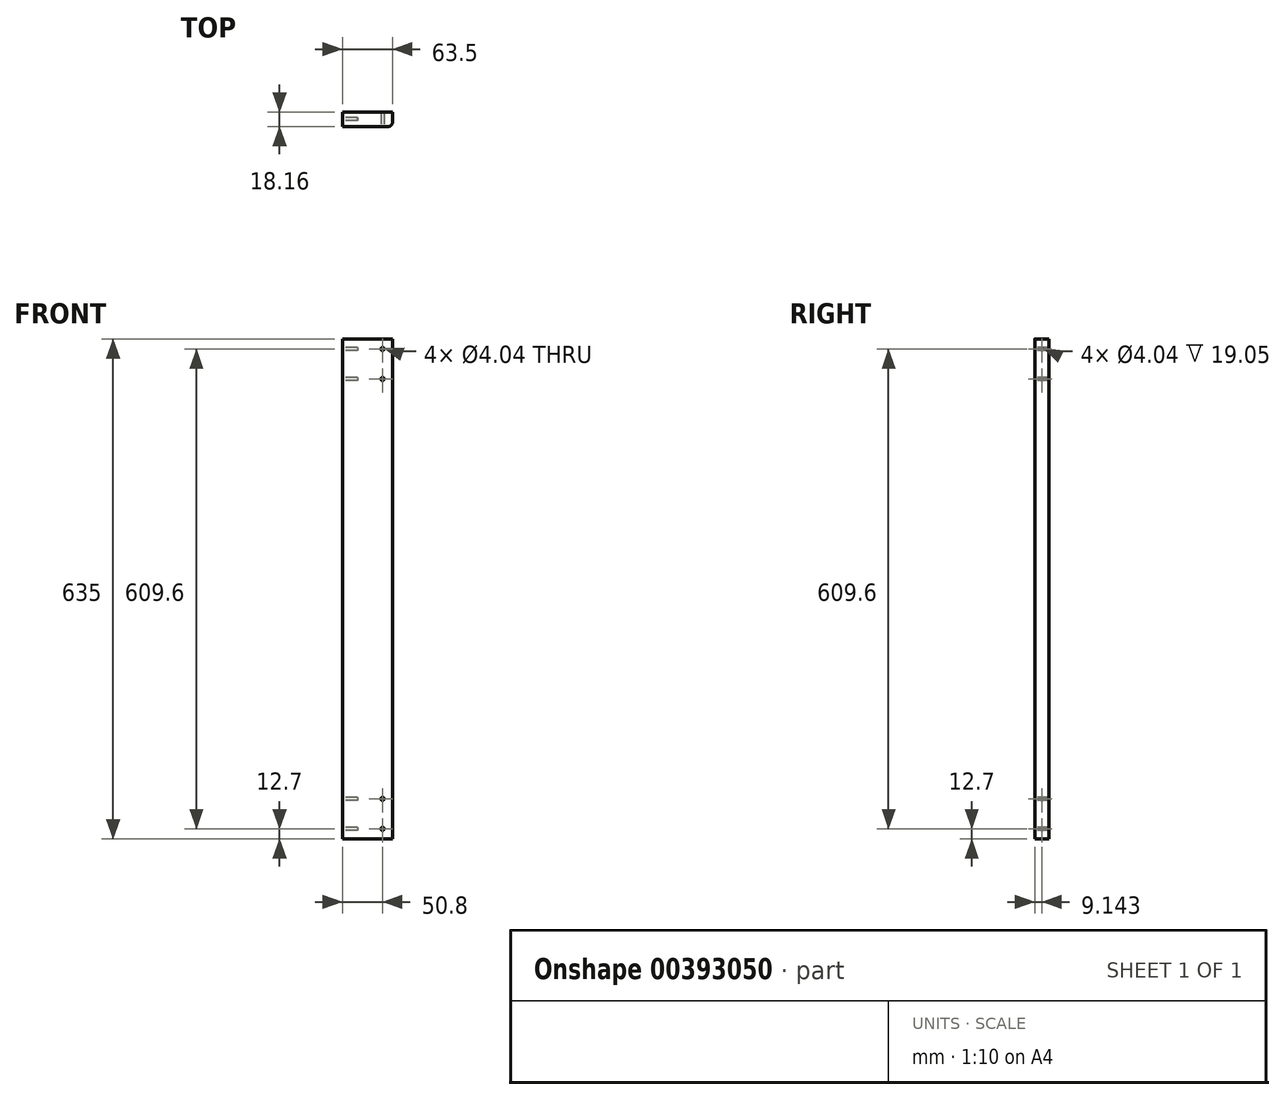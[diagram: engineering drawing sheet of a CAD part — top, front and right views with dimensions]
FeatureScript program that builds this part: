
annotation { "Feature Type Name" : "Feature", "Feature Type Description" : "" }
export const myFeature = defineFeature(function(context is Context, id is Id, definition is map)
    precondition{}
    {
        {
            var Q0;
            Q0=qCreatedBy(makeId("Front.planeOp"),FACE);
            var sketch = newSketch(context, id + "F0", { "sketchPlane" : qUnion([Q0])});
            skLineSegment(sketch, "E0.bottom", {"start": v(0, 0) * mm, "end": v(63.5, 0) * mm});
            skLineSegment(sketch, "E0.top", {"start": v(0, -635) * mm, "end": v(63.5, -635) * mm});
            skLineSegment(sketch, "E0.left", {"start": v(0, 0) * mm, "end": v(0, -635) * mm});
            skLineSegment(sketch, "E0.right", {"start": v(63.5, 0) * mm, "end": v(63.5, -635) * mm});
            skSolve(sketch);
        }
        {
            var Q0;
            Q0 = qSketchRegion(id + "F0", true);
            extrude(context, id + "F1", {"entities" : qUnion([Q0]), "depth" : 18.16 * mm});
        }
        {
            var Q0;
            Q0=makeQuery(id+"F1.opExtrude","CAP_FACE",FACE,{"disambiguationData":[OSD([sQuery(id+"F0.wireOp",EDGE,"E0.bottom"),sQuery(id+"F0.wireOp",EDGE,"E0.top"),sQuery(id+"F0.wireOp",EDGE,"E0.left"),sQuery(id+"F0.wireOp",EDGE,"E0.right")])],"isStart":false});
            var sketch = newSketch(context, id + "F2", { "sketchPlane" : qUnion([Q0])});
            skCircle(sketch, "E1", {"center": v(50.8, -12.7) * mm, "radius": 2.02 * mm});
            skCircle(sketch, "E2", {"center": v(50.8, -50.8) * mm, "radius": 2.02 * mm});
            skCircle(sketch, "E3", {"center": v(50.8, -622.3) * mm, "radius": 2.02 * mm});
            skCircle(sketch, "E4", {"center": v(50.8, -584.2) * mm, "radius": 2.02 * mm});
            skSolve(sketch);
        }
        {
            var Q0;
            Q0 = qSketchRegion(id + "F2", true);
            extrude(context, id + "F3", {"entities" : qUnion([Q0]), "operationType" : NewBodyOperationType.REMOVE, "endBound" : BoundingType.THROUGH_ALL, "oppositeDirection" : true, "depth" : 25.4 * mm});
        }
        {
            var Q0;
            Q0=makeQuery(id+"F1.opExtrude","SWEPT_FACE",FACE,{"disambiguationData":[OSD([sQuery(id+"F0.wireOp",EDGE,"E0.left")])]});
            var sketch = newSketch(context, id + "F4", { "sketchPlane" : qUnion([Q0])});
            skCircle(sketch, "E5", {"center": v(9.02, -12.7) * mm, "radius": 2.02 * mm});
            skCircle(sketch, "E6", {"center": v(9.02, -50.8) * mm, "radius": 2.02 * mm});
            skCircle(sketch, "E7", {"center": v(9.02, -622.3) * mm, "radius": 2.02 * mm});
            skCircle(sketch, "E8", {"center": v(9.02, -584.2) * mm, "radius": 2.02 * mm});
            skSolve(sketch);
        }
        {
            var Q0;
            Q0 = qSketchRegion(id + "F4", true);
            extrude(context, id + "F5", {"entities" : qUnion([Q0]), "operationType" : NewBodyOperationType.REMOVE, "oppositeDirection" : true, "depth" : 19.05 * mm});
        }
        {
            var Q0;
            Q0=makeQuery(id+"F1.opExtrude","CAP_EDGE",EDGE,{"disambiguationData":[OSD([sQuery(id+"F0.wireOp",EDGE,"E0.right")])],"isStart":false});
            fillet(context, id + "F6", {"entities" : qUnion([Q0]), "radius" : 5.08 * mm, "tangentPropagation" : true, "allowEdgeOverflow" : false});
        }
    });
